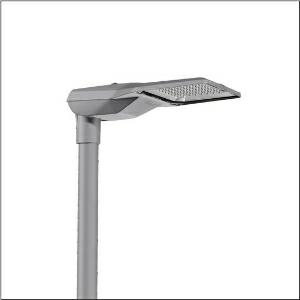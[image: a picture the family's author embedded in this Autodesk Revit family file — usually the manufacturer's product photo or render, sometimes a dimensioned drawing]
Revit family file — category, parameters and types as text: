
# Revit family: streetlight_sl_21_midi___st1_5a_5xe3p43s08mb_00aa
name_source: partatom
category: Lighting Fixtures
units: mm (PartAtom-declared; Revit-internal decimal feet)

## family parameters
Cut with Voids When Loaded = No
Host = Face
Light Source = No
Part Type = Normal
Room Calculation Point = No
Round Connector Dimension = Use Diameter
Shared = No

## types (1)
- --- (1 x LED, 19830 lm, 147 W, 4000K)
    Apparent Load = 147 VA
    CIE Flux Codes = 22 53 95 100 100
    Color Rendering = 70
    Color Temperature = 4000K
    Default Elevation = 1800 mm
    Description = Streetlight SL 21 midi, mast luminaire, primary light control with lens, of PMMA, primary optical cover: cover, of toughened safety glass, transparent, light distribution: ST1.5a, light emission: direct distribution, primary light characteristic: asymmetric, installation type: side-entry, post-top, LED, High Power LED, rated luminous flux: 19.830lm, luminous efficacy: 135lm/W, light colour: 740, colour temperature: 4000K, control gear: D4i, control: overheat protection, constant luminous flux control, time-dependent luminous flux control, flexible luminous flux parameterisation, pre-setting: logarithmic dimming characteristic, mains connection: 230..240V, AC, 50/60Hz, start of lifetime: 147W, end of service life: 155W, reduction: 65W, luminaire housing, of diecast aluminium, powder-coated, SITECO metallic grey (DB 702S), corrosivity category C5 high according to DIN EN ISO 12944, please order mast flange separately, inclination adjustable: 0°, 5°, 10°, 15°, sealing non-destructively replaceable, multi-level sealing system, length: 644mm, width: 335mm, height: 110mm, mast flange for spigot size: 42mm (side-entry): 5XC10008XM4, 60/48mm (side-entry/post-top): 5XC10108XM2, 76/60mm (side-entry/post-top): 5XC10108XM1, mounting height: 4..8m, Smart Interface above, protection rating (complete): IP66, insulation class (complete): insulation class II (safety insulation), certification: CE, ENEC, ENEC+, VDE, impact resistance: IK10, permissible operating ambient temperature for outdoor applications: -40..+50°C, standard-compliant lighting for roads and squares, packaging unit: 1 piece

Light Distribution: ST1.5a
    Height = 111 mm
    Lamp = 1 x LED
    Lamp Light Flux = 19830 lm
    Lamp Power = 147 W
    Lamp count = 1
    Length = 644 mm
    Luminous efficacy = 135 lm/W
    Manufacturer = Siteco
    ModVariant = No
    Model = 5XE3P43S08MB
    Number of Poles = 1
    OnlyDefault = Yes
    Power Factor = 1
    Product Name = Streetlight SL 21 midi | ST1.5a
    Product group = mast luminaire | pylon top
    ProductGroupID = 6100
    Protection Class = Protection class II
    Protection Degree = IP 66
    RLX_Detail_Level = 1
    RLX_Emergency_Light_Flux = 0 lm
    RLX_Emergency_Type = 0
    RLX_Emergency_Type_DB = No
    RlxData = <blob elided: 30389 chars, md5=0a0e5e92>
    Socket = socket
    Standby Power = 0 W
    System Light Flux = 19830 lm
    System Power = 147 W
    Type Comments = factory setting: luminous flux: 100 % | dim-lin: 254 | 750 mA
    Type Image = l_1004302.jpg
    URL = http://relux.com
    VarID = @adj_175621
    Voltage = 0 V
    Weight = 0.00 kg
    Width = 336 mm

## geometry (parser evidence)
native form markers: Blend x4, Sweep x9
no freeform markers — native parametric forms only
